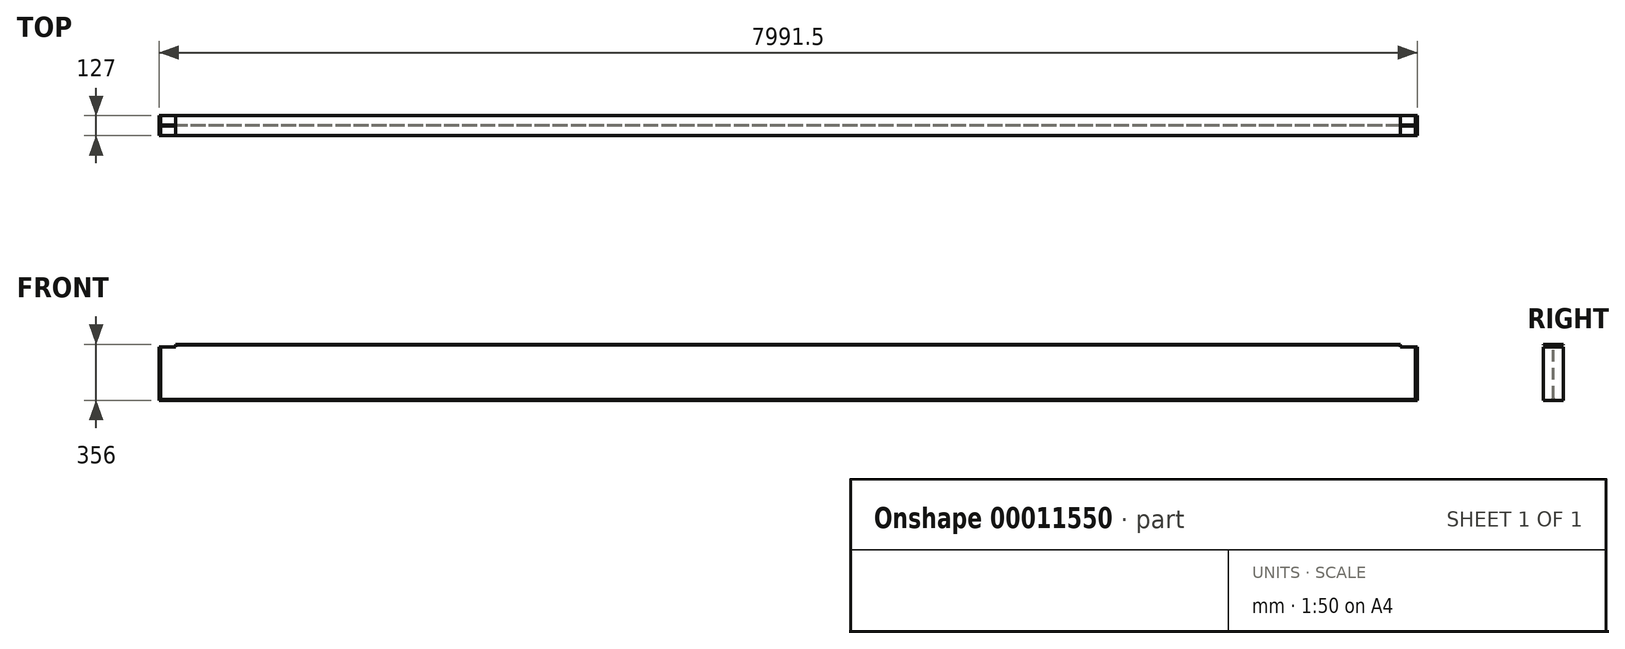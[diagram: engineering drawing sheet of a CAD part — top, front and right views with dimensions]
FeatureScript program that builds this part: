
annotation { "Feature Type Name" : "Feature", "Feature Type Description" : "" }
export const myFeature = defineFeature(function(context is Context, id is Id, definition is map)
    precondition{}
    {
        {
            var Q0;
            Q0=qCreatedBy(makeId("Right.planeOp"),FACE);
            var sketch = newSketch(context, id + "F0", { "sketchPlane" : qUnion([Q0])});
            skLineSegment(sketch, "E0.rect.bottom", {"start": v(63.5, 178) * mm, "end": v(-63.5, 178) * mm});
            skLineSegment(sketch, "E0.rect.top", {"start": v(63.5, -178) * mm, "end": v(-63.5, -178) * mm});
            skLineSegment(sketch, "E0.rect.left", {"start": v(63.5, 178) * mm, "end": v(63.5, 172) * mm});
            skLineSegment(sketch, "E0.rect.right", {"start": v(-63.5, 178) * mm, "end": v(-63.5, 172) * mm});
            skPoint(sketch, "E0.rect.middle", {"position": v(0, 0) * mm});
            skLineSegment(sketch, "E1.0", {"start": v(63.5, 172) * mm, "end": v(13, 172) * mm});
            skLineSegment(sketch, "E2.0", {"start": v(63.5, -172) * mm, "end": v(13, -172) * mm});
            skLineSegment(sketch, "E3.0", {"start": v(-3, 162) * mm, "end": v(-3, -162) * mm});
            skLineSegment(sketch, "E4.0", {"start": v(3, 162) * mm, "end": v(3, -162) * mm});
            skLineSegment(sketch, "E5.trimOffspring", {"start": v(-13, -172) * mm, "end": v(-63.5, -172) * mm});
            skLineSegment(sketch, "E6.trimOffspring", {"start": v(-13, 172) * mm, "end": v(-63.5, 172) * mm});
            skPoint(sketch, "E7.visualSharp", {"position": v(-3, 172) * mm});
            skArc(sketch, "E7.filletArc", {"start": v(-3, 162) * mm, "mid": v(-5.93, 169.07) * mm, "end": v(-13, 172) * mm});
            skPoint(sketch, "E8.visualSharp", {"position": v(3, 172) * mm});
            skArc(sketch, "E8.filletArc", {"start": v(13, 172) * mm, "mid": v(5.93, 169.07) * mm, "end": v(3, 162) * mm});
            skPoint(sketch, "E9.visualSharp", {"position": v(-3, -172) * mm});
            skArc(sketch, "E9.filletArc", {"start": v(-13, -172) * mm, "mid": v(-5.93, -169.07) * mm, "end": v(-3, -162) * mm});
            skPoint(sketch, "E10.visualSharp", {"position": v(3, -172) * mm});
            skArc(sketch, "E10.filletArc", {"start": v(3, -162) * mm, "mid": v(5.93, -169.07) * mm, "end": v(13, -172) * mm});
            skLineSegment(sketch, "E11.trimOffspring", {"start": v(-63.5, -172) * mm, "end": v(-63.5, -178) * mm});
            skLineSegment(sketch, "E12.trimOffspring", {"start": v(63.5, -172) * mm, "end": v(63.5, -178) * mm});
            skSolve(sketch);
        }
        {
            var Q0;
            Q0 = qSketchRegion(id + "F0", true);
            extrude(context, id + "F1", {"entities" : qUnion([Q0]), "endBound" : BoundingType.SYMMETRIC, "depth" : 7991.5 * mm});
        }
        {
            var Q0;
            Q0=makeQuery(id+"F1.opExtrude","CAP_FACE",FACE,{"disambiguationData":[OSD([sQuery(id+"F0.wireOp",EDGE,"E0.rect.bottom"),sQuery(id+"F0.wireOp",EDGE,"E0.rect.top"),sQuery(id+"F0.wireOp",EDGE,"E0.rect.left"),sQuery(id+"F0.wireOp",EDGE,"E0.rect.right"),sQuery(id+"F0.wireOp",EDGE,"E1.0"),sQuery(id+"F0.wireOp",EDGE,"E2.0"),sQuery(id+"F0.wireOp",EDGE,"E3.0"),sQuery(id+"F0.wireOp",EDGE,"E4.0"),sQuery(id+"F0.wireOp",EDGE,"E5.trimOffspring"),sQuery(id+"F0.wireOp",EDGE,"E6.trimOffspring"),sQuery(id+"F0.wireOp",EDGE,"E7.filletArc"),sQuery(id+"F0.wireOp",EDGE,"E8.filletArc"),sQuery(id+"F0.wireOp",EDGE,"E9.filletArc"),sQuery(id+"F0.wireOp",EDGE,"E10.filletArc"),sQuery(id+"F0.wireOp",EDGE,"E11.trimOffspring"),sQuery(id+"F0.wireOp",EDGE,"E12.trimOffspring")])],"isStart":false});
            var sketch = newSketch(context, id + "F2", { "sketchPlane" : qUnion([Q0])});
            skLineSegment(sketch, "E13.bottom", {"start": v(-63.5, 178) * mm, "end": v(63.5, 178) * mm});
            skLineSegment(sketch, "E13.top", {"start": v(-63.5, -178) * mm, "end": v(63.5, -178) * mm});
            skLineSegment(sketch, "E13.left", {"start": v(-63.5, 178) * mm, "end": v(-63.5, -178) * mm});
            skLineSegment(sketch, "E13.right", {"start": v(63.5, 178) * mm, "end": v(63.5, -178) * mm});
            skSolve(sketch);
        }
        {
            var Q0;
            Q0=makeQuery(id+"F2.imprint","IMPRINT",FACE,{"disambiguationData":[TD([[makeQuery(id+"F2.imprint","IMPRINT",EDGE,{"derivedFrom":makeQuery(id+"F1.opExtrude","CAP_EDGE",EDGE,{"disambiguationData":[OSD([sQuery(id+"F0.wireOp",EDGE,"E3.0")])],"isStart":false})}),-1.0]])]});
            var Q1;
            {var subQ1=makeQuery(id+"F1.opExtrude","CAP_EDGE",EDGE,{"disambiguationData":[OSD([sQuery(id+"F0.wireOp",EDGE,"E1.0")])],"isStart":false});Q1=makeQuery(id+"F2.imprint","IMPRINT",FACE,{"disambiguationData":[TD([[makeQuery(id+"F2.imprint","IMPRINT",EDGE,{"derivedFrom":subQ1}),1.0]])]});}
            var Q2;
            {var subQ5=sQuery(id+"F2.wireOp",EDGE,"b6c85c3d-8caf-48c7-af72-7e41afa59fa2.bottom");Q2=makeQuery(id+"F2.imprint","IMPRINT",FACE,{"disambiguationData":[TD([[makeQuery(id+"F2.imprint","IMPRINT",EDGE,{"derivedFrom":subQ5}),1.0]])]});}
            var Q3;
            {var subQ5=sQuery(id+"F2.wireOp",EDGE,"c5d3591f-d078-4e24-917f-32848cda5116.bottom");Q3=makeQuery(id+"F2.imprint","IMPRINT",FACE,{"disambiguationData":[TD([[makeQuery(id+"F2.imprint","IMPRINT",EDGE,{"derivedFrom":subQ5}),-1.0]])]});}
            var Q4;
            {var subQ1=makeQuery(id+"F1.opExtrude","CAP_EDGE",EDGE,{"disambiguationData":[OSD([sQuery(id+"F0.wireOp",EDGE,"E2.0")])],"isStart":false});Q4=makeQuery(id+"F2.imprint","IMPRINT",FACE,{"disambiguationData":[TD([[makeQuery(id+"F2.imprint","IMPRINT",EDGE,{"derivedFrom":subQ1}),-1.0]])]});}
            var Q5;
            {var subQ5=sQuery(id+"F2.wireOp",EDGE,"E13.bottom");Q5=makeQuery(id+"F2.imprint","IMPRINT",FACE,{"disambiguationData":[TD([[makeQuery(id+"F2.imprint","IMPRINT",EDGE,{"derivedFrom":subQ5}),1.0]])]});}
            extrude(context, id + "F3", {"entities" : qUnion([Q0, Q1, Q2, Q3, Q4, Q5]), "operationType" : NewBodyOperationType.ADD, "oppositeDirection" : true, "depth" : 11.05 * mm});
        }
        {
            var Q0;
            Q0=makeQuery(id+"F1.opExtrude","CAP_FACE",FACE,{"disambiguationData":[OSD([sQuery(id+"F0.wireOp",EDGE,"E0.rect.bottom"),sQuery(id+"F0.wireOp",EDGE,"E0.rect.top"),sQuery(id+"F0.wireOp",EDGE,"E0.rect.left"),sQuery(id+"F0.wireOp",EDGE,"E0.rect.right"),sQuery(id+"F0.wireOp",EDGE,"E1.0"),sQuery(id+"F0.wireOp",EDGE,"E2.0"),sQuery(id+"F0.wireOp",EDGE,"E3.0"),sQuery(id+"F0.wireOp",EDGE,"E4.0"),sQuery(id+"F0.wireOp",EDGE,"E5.trimOffspring"),sQuery(id+"F0.wireOp",EDGE,"E6.trimOffspring"),sQuery(id+"F0.wireOp",EDGE,"E7.filletArc"),sQuery(id+"F0.wireOp",EDGE,"E8.filletArc"),sQuery(id+"F0.wireOp",EDGE,"E9.filletArc"),sQuery(id+"F0.wireOp",EDGE,"E10.filletArc"),sQuery(id+"F0.wireOp",EDGE,"E11.trimOffspring"),sQuery(id+"F0.wireOp",EDGE,"E12.trimOffspring")])],"isStart":true});
            var sketch = newSketch(context, id + "F4", { "sketchPlane" : qUnion([Q0])});
            skLineSegment(sketch, "E14.bottom", {"start": v(-63.5, -178) * mm, "end": v(63.5, -178) * mm});
            skLineSegment(sketch, "E14.top", {"start": v(-63.5, 178) * mm, "end": v(63.5, 178) * mm});
            skLineSegment(sketch, "E14.left", {"start": v(-63.5, -178) * mm, "end": v(-63.5, 178) * mm});
            skLineSegment(sketch, "E14.right", {"start": v(63.5, -178) * mm, "end": v(63.5, 178) * mm});
            skSolve(sketch);
        }
        {
            var Q0;
            {var subQ1=makeQuery(id+"F1.opExtrude","CAP_EDGE",EDGE,{"disambiguationData":[OSD([sQuery(id+"F0.wireOp",EDGE,"E1.0")])],"isStart":true});Q0=makeQuery(id+"F4.imprint","IMPRINT",FACE,{"disambiguationData":[TD([[makeQuery(id+"F4.imprint","IMPRINT",EDGE,{"derivedFrom":subQ1}),-1.0]])]});}
            var Q1;
            {var subQ6=sQuery(id+"F4.wireOp",EDGE,"E14.bottom");Q1=makeQuery(id+"F4.imprint","IMPRINT",FACE,{"disambiguationData":[TD([[makeQuery(id+"F4.imprint","IMPRINT",EDGE,{"derivedFrom":subQ6}),1.0]])]});}
            var Q2;
            Q2=makeQuery(id+"F4.imprint","IMPRINT",FACE,{"disambiguationData":[TD([[makeQuery(id+"F4.imprint","IMPRINT",EDGE,{"derivedFrom":makeQuery(id+"F1.opExtrude","CAP_EDGE",EDGE,{"disambiguationData":[OSD([sQuery(id+"F0.wireOp",EDGE,"E3.0")])],"isStart":true})}),1.0]])]});
            extrude(context, id + "F5", {"entities" : qUnion([Q0, Q1, Q2]), "operationType" : NewBodyOperationType.ADD, "oppositeDirection" : true, "depth" : 11.05 * mm});
        }
        {
            var Q0;
            Q0=makeQuery(id+"F3.boolean.opBoolean","MERGE",FACE,{"derivedFrom":[makeQuery(id+"F1.opExtrude","CAP_FACE",FACE,{"disambiguationData":[OSD([sQuery(id+"F0.wireOp",EDGE,"E0.rect.bottom"),sQuery(id+"F0.wireOp",EDGE,"E0.rect.top"),sQuery(id+"F0.wireOp",EDGE,"E0.rect.left"),sQuery(id+"F0.wireOp",EDGE,"E0.rect.right"),sQuery(id+"F0.wireOp",EDGE,"E1.0"),sQuery(id+"F0.wireOp",EDGE,"E2.0"),sQuery(id+"F0.wireOp",EDGE,"E3.0"),sQuery(id+"F0.wireOp",EDGE,"E4.0"),sQuery(id+"F0.wireOp",EDGE,"E5.trimOffspring"),sQuery(id+"F0.wireOp",EDGE,"E6.trimOffspring"),sQuery(id+"F0.wireOp",EDGE,"E7.filletArc"),sQuery(id+"F0.wireOp",EDGE,"E8.filletArc"),sQuery(id+"F0.wireOp",EDGE,"E9.filletArc"),sQuery(id+"F0.wireOp",EDGE,"E10.filletArc"),sQuery(id+"F0.wireOp",EDGE,"E11.trimOffspring"),sQuery(id+"F0.wireOp",EDGE,"E12.trimOffspring")])],"isStart":false}),makeQuery(id+"F3.opExtrude","CAP_FACE",FACE,{"disambiguationData":[OSD([sQuery(id+"F2.wireOp",EDGE,"E13.bottom"),sQuery(id+"F2.wireOp",EDGE,"E13.top"),sQuery(id+"F2.wireOp",EDGE,"E13.left"),sQuery(id+"F2.wireOp",EDGE,"E13.right")])],"isStart":true})]});
            var sketch = newSketch(context, id + "F6", { "sketchPlane" : qUnion([Q0])});
            skLineSegment(sketch, "E15.bottom", {"start": v(-63.5, 178) * mm, "end": v(63.5, 178) * mm});
            skLineSegment(sketch, "E15.top", {"start": v(-63.5, 162) * mm, "end": v(63.5, 162) * mm});
            skLineSegment(sketch, "E15.left", {"start": v(-63.5, 178) * mm, "end": v(-63.5, 162) * mm});
            skLineSegment(sketch, "E15.right", {"start": v(63.5, 178) * mm, "end": v(63.5, 162) * mm});
            skSolve(sketch);
        }
        {
            var Q0;
            Q0 = qSketchRegion(id + "F6", true);
            extrude(context, id + "F7", {"entities" : qUnion([Q0]), "operationType" : NewBodyOperationType.REMOVE, "oppositeDirection" : true, "depth" : 106 * mm});
        }
        {
            var Q0;
            Q0=makeQuery(id+"F5.boolean.opBoolean","MERGE",FACE,{"derivedFrom":[makeQuery(id+"F1.opExtrude","CAP_FACE",FACE,{"disambiguationData":[OSD([sQuery(id+"F0.wireOp",EDGE,"E0.rect.bottom"),sQuery(id+"F0.wireOp",EDGE,"E0.rect.top"),sQuery(id+"F0.wireOp",EDGE,"E0.rect.left"),sQuery(id+"F0.wireOp",EDGE,"E0.rect.right"),sQuery(id+"F0.wireOp",EDGE,"E1.0"),sQuery(id+"F0.wireOp",EDGE,"E2.0"),sQuery(id+"F0.wireOp",EDGE,"E3.0"),sQuery(id+"F0.wireOp",EDGE,"E4.0"),sQuery(id+"F0.wireOp",EDGE,"E5.trimOffspring"),sQuery(id+"F0.wireOp",EDGE,"E6.trimOffspring"),sQuery(id+"F0.wireOp",EDGE,"E7.filletArc"),sQuery(id+"F0.wireOp",EDGE,"E8.filletArc"),sQuery(id+"F0.wireOp",EDGE,"E9.filletArc"),sQuery(id+"F0.wireOp",EDGE,"E10.filletArc"),sQuery(id+"F0.wireOp",EDGE,"E11.trimOffspring"),sQuery(id+"F0.wireOp",EDGE,"E12.trimOffspring")])],"isStart":true}),makeQuery(id+"F5.opExtrude","CAP_FACE",FACE,{"disambiguationData":[OSD([sQuery(id+"F4.wireOp",EDGE,"E14.bottom"),sQuery(id+"F4.wireOp",EDGE,"E14.top"),sQuery(id+"F4.wireOp",EDGE,"E14.left"),sQuery(id+"F4.wireOp",EDGE,"E14.right")])],"isStart":true})]});
            var sketch = newSketch(context, id + "F8", { "sketchPlane" : qUnion([Q0])});
            skLineSegment(sketch, "E16.bottom", {"start": v(-63.5, 178) * mm, "end": v(63.5, 178) * mm});
            skLineSegment(sketch, "E16.top", {"start": v(-63.5, 162) * mm, "end": v(63.5, 162) * mm});
            skLineSegment(sketch, "E16.left", {"start": v(-63.5, 178) * mm, "end": v(-63.5, 162) * mm});
            skLineSegment(sketch, "E16.right", {"start": v(63.5, 178) * mm, "end": v(63.5, 162) * mm});
            skSolve(sketch);
        }
        {
            var Q0;
            Q0 = qSketchRegion(id + "F8", true);
            extrude(context, id + "F9", {"entities" : qUnion([Q0]), "operationType" : NewBodyOperationType.REMOVE, "oppositeDirection" : true, "depth" : 106 * mm});
        }
    });
